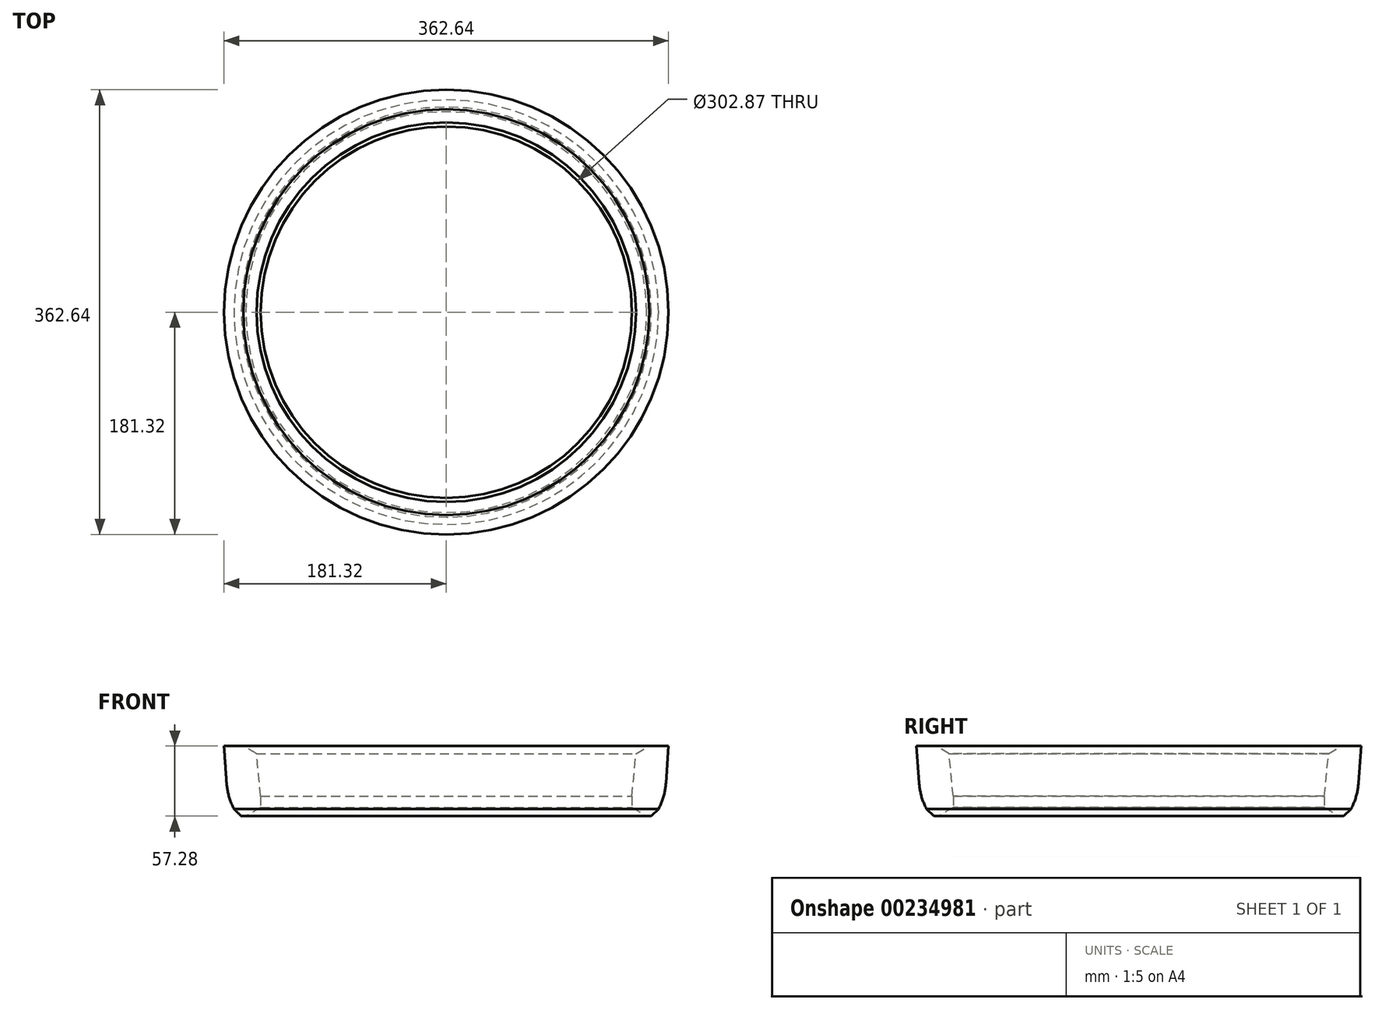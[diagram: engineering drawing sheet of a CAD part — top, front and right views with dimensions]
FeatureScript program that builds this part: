
annotation { "Feature Type Name" : "Feature", "Feature Type Description" : "" }
export const myFeature = defineFeature(function(context is Context, id is Id, definition is map)
    precondition{}
    {
        {
            var Q0;
            Q0=qCreatedBy(makeId("Front.planeOp"),FACE);
            var sketch = newSketch(context, id + "F0", { "sketchPlane" : qUnion([Q0])});
            skLineSegment(sketch, "E0", {"start": v(0, 0) * mm, "end": v(0, 60.64) * mm});
            skLineSegment(sketch, "E1", {"start": v(-163.5, 0) * mm, "end": v(-167.3, 0) * mm});
            skLineSegment(sketch, "E2", {"start": v(-179.2, 27.03) * mm, "end": v(-181.32, 57.28) * mm});
            skLineSegment(sketch, "E3", {"start": v(-167.3, 0) * mm, "end": v(-173.16, 5.87) * mm});
            skLineSegment(sketch, "E4", {"start": v(-163.5, 0) * mm, "end": v(-151.44, 6.96) * mm});
            skLineSegment(sketch, "E5", {"start": v(-165.56, 57.28) * mm, "end": v(-154.79, 51.06) * mm});
            skLineSegment(sketch, "E6", {"start": v(-154.79, 51.06) * mm, "end": v(-151.44, 16.27) * mm});
            skLineSegment(sketch, "E7.trimOffspring", {"start": v(-151.44, 16.27) * mm, "end": v(-151.44, 6.96) * mm});
            skLineSegment(sketch, "E8.trimOffspring", {"start": v(-165.56, 57.28) * mm, "end": v(-181.32, 57.28) * mm});
            skArc(sketch, "E9", {"start": v(-179.2, 27.03) * mm, "mid": v(-177.3, 16.13) * mm, "end": v(-173.16, 5.87) * mm});
            skSolve(sketch);
        }
        {
            var Q0;
            Q0 = qSketchRegion(id + "F0", true);
            var Q1;
            Q1=sQuery(id+"F0.wireOp",EDGE,"E0");
            revolve(context, id + "F1", {"entities" : qUnion([Q0]), "axis" : qUnion([Q1]), "revolveType" : RevolveType.FULL});
        }
    });
